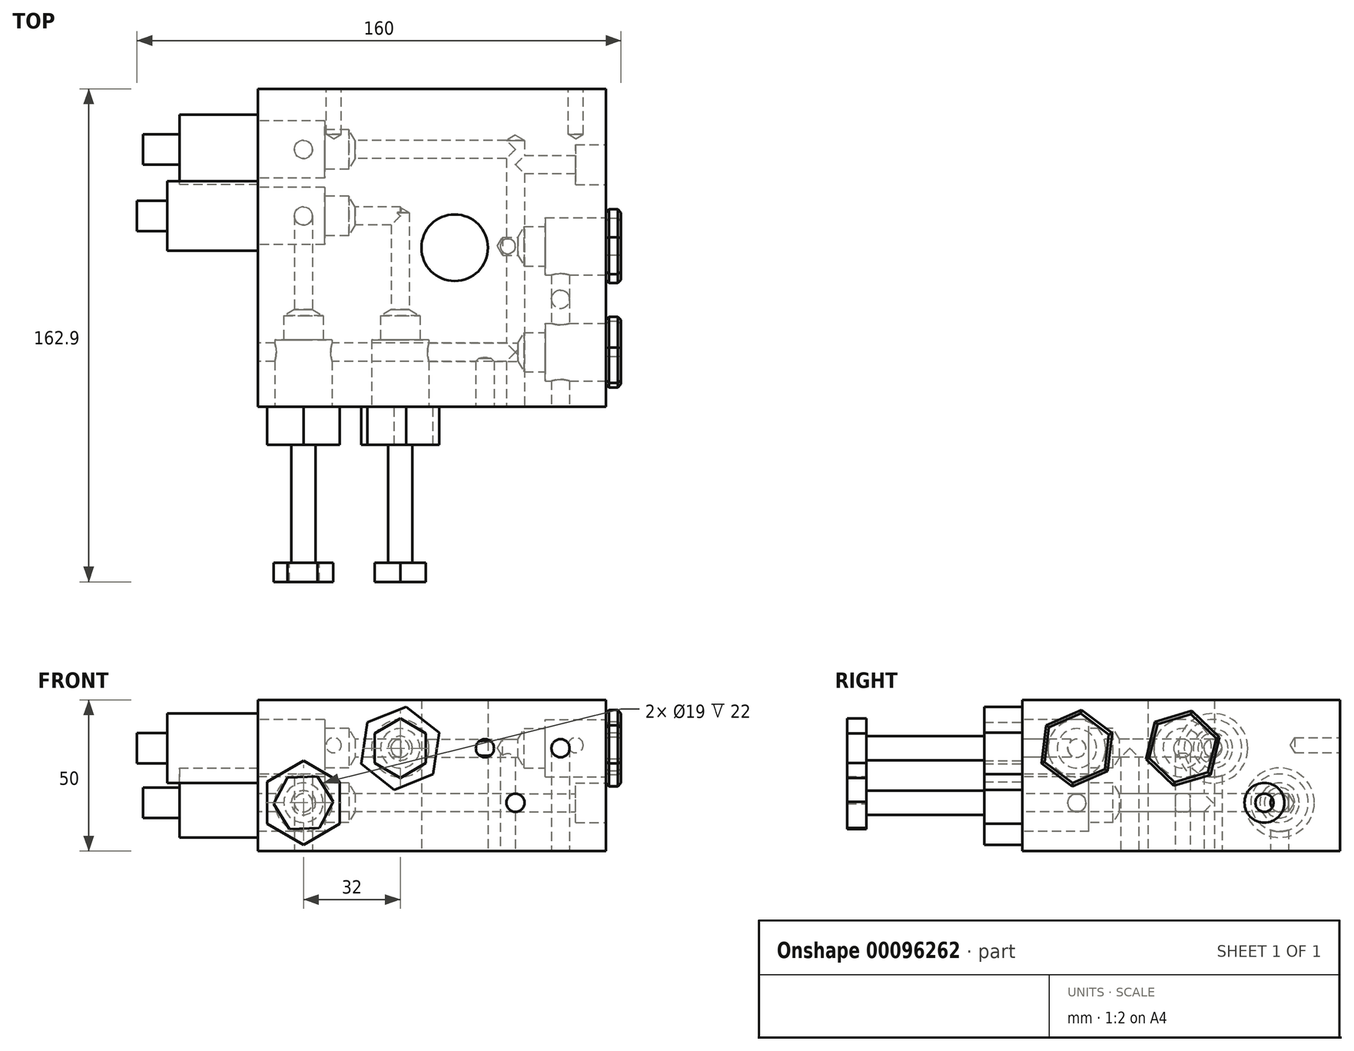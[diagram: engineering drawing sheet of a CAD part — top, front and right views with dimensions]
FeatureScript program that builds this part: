
annotation { "Feature Type Name" : "Feature", "Feature Type Description" : "" }
export const myFeature = defineFeature(function(context is Context, id is Id, definition is map)
    precondition{}
    {
        {
            var Q0;
            Q0=qCreatedBy(makeId("Top.planeOp"),FACE);
            var sketch = newSketch(context, id + "F0", { "sketchPlane" : qUnion([Q0])});
            skLineSegment(sketch, "E0.rect.bottom", {"start": v(50, 52.5) * mm, "end": v(-65, 52.5) * mm});
            skLineSegment(sketch, "E0.rect.top", {"start": v(50, -52.5) * mm, "end": v(-65, -52.5) * mm});
            skLineSegment(sketch, "E0.rect.left", {"start": v(50, 52.5) * mm, "end": v(50, -52.5) * mm});
            skLineSegment(sketch, "E0.rect.right", {"start": v(-65, 52.5) * mm, "end": v(-65, -52.5) * mm});
            skPoint(sketch, "E0.rect.middle", {"position": v(0, 0) * mm});
            skSolve(sketch);
        }
        {
            var Q0;
            Q0=makeQuery(id+"F0.imprint","IMPRINT",FACE,{"disambiguationData":[TD([[makeQuery(id+"F0.imprint","IMPRINT",EDGE,{"derivedFrom":sQuery(id+"F0.wireOp",EDGE,"E0.rect.bottom")}),1.0]])]});
            var Q1;
            Q1=makeQuery(id+"F0.imprint","IMPRINT",FACE,{"disambiguationData":[TD([[makeQuery(id+"F0.imprint","IMPRINT",EDGE,{"derivedFrom":sQuery(id+"F0.wireOp",EDGE,"7588558b-6d4b-4371-8287-17bf13519ebf.1.0.0")}),1.0]])]});
            var Q2;
            Q2=makeQuery(id+"F0.imprint","IMPRINT",FACE,{"disambiguationData":[TD([[makeQuery(id+"F0.imprint","IMPRINT",EDGE,{"derivedFrom":sQuery(id+"F0.wireOp",EDGE,"7588558b-6d4b-4371-8287-17bf13519ebf.1.1.0")}),1.0]])]});
            var Q3;
            Q3=makeQuery(id+"F0.imprint","IMPRINT",FACE,{"disambiguationData":[TD([[makeQuery(id+"F0.imprint","IMPRINT",EDGE,{"derivedFrom":sQuery(id+"F0.wireOp",EDGE,"f2f94a69-6f03-48d5-8e05-4ef8c2e551b9")}),1.0]])]});
            var Q4;
            Q4=makeQuery(id+"F0.imprint","IMPRINT",FACE,{"disambiguationData":[TD([[makeQuery(id+"F0.imprint","IMPRINT",EDGE,{"derivedFrom":sQuery(id+"F0.wireOp",EDGE,"7588558b-6d4b-4371-8287-17bf13519ebf.0.1.0")}),1.0]])]});
            extrude(context, id + "F1", {"entities" : qUnion([Q0, Q1, Q2, Q3, Q4]), "depth" : 50 * mm});
        }
        {
            var Q0;
            Q0=makeQuery(id+"F1.opExtrude","CAP_FACE",FACE,{"disambiguationData":[OSD([sQuery(id+"F0.wireOp",EDGE,"E0.rect.bottom"),sQuery(id+"F0.wireOp",EDGE,"E0.rect.top"),sQuery(id+"F0.wireOp",EDGE,"E0.rect.left"),sQuery(id+"F0.wireOp",EDGE,"E0.rect.right"),sQuery(id+"F0.wireOp",EDGE,"fc206ab4-4ad2-4e77-9b30-4fb9f0a5357b")])],"isStart":true});
            var sketch = newSketch(context, id + "F2", { "sketchPlane" : qUnion([Q0])});
            skCircle(sketch, "E1", {"center": v(11.74, 13.3) * mm, "radius": 2.1 * mm});
            skCircle(sketch, "E2", {"center": v(-6.03, -26.8) * mm, "radius": 2.1 * mm});
            skCircle(sketch, "E3", {"center": v(17.59, -0.5) * mm, "radius": 2.5 * mm});
            skPoint(sketch, "E4", {"position": v(-50, -10.5) * mm});
            skPoint(sketch, "E5", {"position": v(35, 17) * mm});
            skPoint(sketch, "E6", {"position": v(-50, -32.5) * mm});
            skSolve(sketch);
        }
        {
            var Q0;
            Q0=sQuery(id+"F2.wireOp",VERTEX,"E3.center");
            var Q1;
            Q1=makeQuery(id+"F1.opExtrude","SWEPT_BODY",BODY,{"disambiguationData":[OSD([sQuery(id+"F0.wireOp",EDGE,"E0.rect.bottom"),sQuery(id+"F0.wireOp",EDGE,"E0.rect.top"),sQuery(id+"F0.wireOp",EDGE,"E0.rect.left"),sQuery(id+"F0.wireOp",EDGE,"E0.rect.right"),sQuery(id+"F0.wireOp",EDGE,"fc206ab4-4ad2-4e77-9b30-4fb9f0a5357b")])]});
            hole(context, id + "F3", {"style" : HoleStyle.SIMPLE, "holeDiameter" : 5 * mm, "endStyle" : HoleEndStyle.BLIND, "holeDepth" : 35 * mm, "locations" : qUnion([Q0]), "scope" : qUnion([Q1])});
        }
        {
            var Q0;
            Q0=makeQuery(id+"F1.opExtrude","SWEPT_FACE",FACE,{"disambiguationData":[OSD([sQuery(id+"F0.wireOp",EDGE,"E0.rect.bottom")])]});
            var sketch = newSketch(context, id + "F4", { "sketchPlane" : qUnion([Q0])});
            skLineSegment(sketch, "E7", {"start": v(65, 16) * mm, "end": v(-50, 16) * mm, "construction": true});
            skPoint(sketch, "E8", {"position": v(-20.09, 16) * mm});
            skPoint(sketch, "E9", {"position": v(45, 16) * mm});
            skSolve(sketch);
        }
        {
            var Q0;
            Q0=makeQuery(id+"F1.opExtrude","SWEPT_FACE",FACE,{"disambiguationData":[OSD([sQuery(id+"F0.wireOp",EDGE,"E0.rect.left")])]});
            var sketch = newSketch(context, id + "F5", { "sketchPlane" : qUnion([Q0])});
            skLineSegment(sketch, "E10", {"start": v(-34.5, 34) * mm, "end": v(0.5, 34) * mm, "construction": true});
            skPoint(sketch, "E11", {"position": v(0.5, 34) * mm});
            skPoint(sketch, "E12", {"position": v(-34.5, 34) * mm});
            skPoint(sketch, "E13.orphan", {"position": v(52.5, 34) * mm});
            skPoint(sketch, "E14", {"position": v(27.5, 16) * mm});
            skCircle(sketch, "E15.cCircle", {"center": v(-34.5, 34) * mm, "radius": 11 * mm, "construction": true});
            skLineSegment(sketch, "E15.0", {"start": v(-44.69, 41.58) * mm, "end": v(-33.03, 46.62) * mm});
            skLineSegment(sketch, "E15.1", {"start": v(-33.03, 46.62) * mm, "end": v(-22.84, 39.03) * mm});
            skLineSegment(sketch, "E15.2", {"start": v(-22.84, 39.03) * mm, "end": v(-24.31, 26.42) * mm});
            skLineSegment(sketch, "E15.3", {"start": v(-24.31, 26.42) * mm, "end": v(-35.97, 21.38) * mm});
            skLineSegment(sketch, "E15.4", {"start": v(-35.97, 21.38) * mm, "end": v(-46.16, 28.97) * mm});
            skLineSegment(sketch, "E15.5", {"start": v(-46.16, 28.97) * mm, "end": v(-44.69, 41.58) * mm});
            skPoint(sketch, "E15.0.midPoint", {"position": v(-38.86, 44.1) * mm});
            skCircle(sketch, "E16.cCircle", {"center": v(0.5, 34) * mm, "radius": 11 * mm, "construction": true});
            skLineSegment(sketch, "E16.0", {"start": v(-8.7, 42.75) * mm, "end": v(3.48, 46.35) * mm});
            skLineSegment(sketch, "E16.1", {"start": v(3.48, 46.35) * mm, "end": v(12.68, 37.6) * mm});
            skLineSegment(sketch, "E16.2", {"start": v(12.68, 37.6) * mm, "end": v(9.7, 25.25) * mm});
            skLineSegment(sketch, "E16.3", {"start": v(9.7, 25.25) * mm, "end": v(-2.48, 21.65) * mm});
            skLineSegment(sketch, "E16.4", {"start": v(-2.48, 21.65) * mm, "end": v(-11.68, 30.4) * mm});
            skLineSegment(sketch, "E16.5", {"start": v(-11.68, 30.4) * mm, "end": v(-8.7, 42.75) * mm});
            skPoint(sketch, "E16.0.midPoint", {"position": v(-2.61, 44.55) * mm});
            skSolve(sketch);
        }
        {
            var Q0;
            Q0=sQuery(id+"F5.wireOp",VERTEX,"E11");
            var Q1;
            Q1=sQuery(id+"F5.wireOp",VERTEX,"E12");
            var Q2;
            Q2=makeQuery(id+"F1.opExtrude","SWEPT_BODY",BODY,{"disambiguationData":[OSD([sQuery(id+"F0.wireOp",EDGE,"E0.rect.bottom"),sQuery(id+"F0.wireOp",EDGE,"E0.rect.top"),sQuery(id+"F0.wireOp",EDGE,"E0.rect.left"),sQuery(id+"F0.wireOp",EDGE,"E0.rect.right"),sQuery(id+"F0.wireOp",EDGE,"fc206ab4-4ad2-4e77-9b30-4fb9f0a5357b")])]});
            hole(context, id + "F6", {"style" : HoleStyle.C_BORE, "endStyle" : HoleEndStyle.BLIND, "holeDiameter" : 13 * mm, "cBoreDiameter" : 19 * mm, "cBoreDepth" : 20 * mm, "holeDepth" : 27 * mm, "locations" : qUnion([Q0, Q1]), "scope" : qUnion([Q2])});
        }
        {
            var Q0;
            Q0=makeQuery(id+"F1.opExtrude","SWEPT_FACE",FACE,{"disambiguationData":[OSD([sQuery(id+"F0.wireOp",EDGE,"E0.rect.top")])]});
            var sketch = newSketch(context, id + "F7", { "sketchPlane" : qUnion([Q0])});
            skLineSegment(sketch, "E17", {"start": v(-65, 34) * mm, "end": v(50, 34) * mm, "construction": true});
            skLineSegment(sketch, "E18", {"start": v(-65, 16) * mm, "end": v(50, 16) * mm, "construction": true});
            skPoint(sketch, "E19", {"position": v(-50, 16) * mm});
            skPoint(sketch, "E20", {"position": v(-18, 34) * mm});
            skPoint(sketch, "E21", {"position": v(35, 34) * mm});
            skPoint(sketch, "E22", {"position": v(10, 34) * mm});
            skPoint(sketch, "E23", {"position": v(20.1, 16) * mm});
            skSolve(sketch);
        }
        {
            var Q0;
            Q0=sQuery(id+"F7.wireOp",VERTEX,"E23");
            var Q1;
            Q1=makeQuery(id+"F1.opExtrude","SWEPT_BODY",BODY,{"disambiguationData":[OSD([sQuery(id+"F0.wireOp",EDGE,"E0.rect.bottom"),sQuery(id+"F0.wireOp",EDGE,"E0.rect.top"),sQuery(id+"F0.wireOp",EDGE,"E0.rect.left"),sQuery(id+"F0.wireOp",EDGE,"E0.rect.right"),sQuery(id+"F0.wireOp",EDGE,"fc206ab4-4ad2-4e77-9b30-4fb9f0a5357b")])]});
            hole(context, id + "F8", {"style" : HoleStyle.SIMPLE, "holeDiameter" : 6 * mm, "endStyle" : HoleEndStyle.BLIND, "holeDepth" : 88 * mm, "locations" : qUnion([Q0]), "scope" : qUnion([Q1])});
        }
        {
            var Q0;
            Q0=makeQuery(id+"F1.opExtrude","SWEPT_FACE",FACE,{"disambiguationData":[OSD([sQuery(id+"F0.wireOp",EDGE,"E0.rect.right")])]});
            var sketch = newSketch(context, id + "F9", { "sketchPlane" : qUnion([Q0])});
            skPoint(sketch, "E24", {"position": v(34.5, 16) * mm});
            skPoint(sketch, "E25", {"position": v(-10.5, 34) * mm});
            skPoint(sketch, "E26", {"position": v(-32.5, 16) * mm});
            skCircle(sketch, "E27", {"center": v(-10.5, 34) * mm, "radius": 11.5 * mm});
            skSolve(sketch);
        }
        {
            var Q0;
            Q0=sQuery(id+"F9.wireOp",VERTEX,"E24");
            var Q1;
            Q1=makeQuery(id+"F1.opExtrude","SWEPT_BODY",BODY,{"disambiguationData":[OSD([sQuery(id+"F0.wireOp",EDGE,"E0.rect.bottom"),sQuery(id+"F0.wireOp",EDGE,"E0.rect.top"),sQuery(id+"F0.wireOp",EDGE,"E0.rect.left"),sQuery(id+"F0.wireOp",EDGE,"E0.rect.right"),sQuery(id+"F0.wireOp",EDGE,"fc206ab4-4ad2-4e77-9b30-4fb9f0a5357b")])]});
            hole(context, id + "F10", {"style" : HoleStyle.SIMPLE, "endStyle" : HoleEndStyle.BLIND, "holeDiameter" : 6 * mm, "holeDepth" : 86 * mm, "locations" : qUnion([Q0]), "scope" : qUnion([Q1])});
        }
        {
            var Q0;
            Q0=sQuery(id+"F7.wireOp",VERTEX,"E19");
            var Q1;
            Q1=sQuery(id+"F7.wireOp",VERTEX,"E20");
            var Q2;
            Q2=makeQuery(id+"F1.opExtrude","SWEPT_BODY",BODY,{"disambiguationData":[OSD([sQuery(id+"F0.wireOp",EDGE,"E0.rect.bottom"),sQuery(id+"F0.wireOp",EDGE,"E0.rect.top"),sQuery(id+"F0.wireOp",EDGE,"E0.rect.left"),sQuery(id+"F0.wireOp",EDGE,"E0.rect.right"),sQuery(id+"F0.wireOp",EDGE,"fc206ab4-4ad2-4e77-9b30-4fb9f0a5357b")])]});
            hole(context, id + "F11", {"style" : HoleStyle.C_BORE, "endStyle" : HoleEndStyle.BLIND, "holeDiameter" : 13 * mm, "cBoreDiameter" : 19 * mm, "cBoreDepth" : 22 * mm, "holeDepth" : 30 * mm, "locations" : qUnion([Q0, Q1]), "scope" : qUnion([Q2])});
        }
        {
            var Q0;
            Q0=sQuery(id+"F7.wireOp",VERTEX,"E19");
            var Q1;
            Q1=makeQuery(id+"F1.opExtrude","SWEPT_BODY",BODY,{"disambiguationData":[OSD([sQuery(id+"F0.wireOp",EDGE,"E0.rect.bottom"),sQuery(id+"F0.wireOp",EDGE,"E0.rect.top"),sQuery(id+"F0.wireOp",EDGE,"E0.rect.left"),sQuery(id+"F0.wireOp",EDGE,"E0.rect.right"),sQuery(id+"F0.wireOp",EDGE,"fc206ab4-4ad2-4e77-9b30-4fb9f0a5357b")])]});
            hole(context, id + "F12", {"style" : HoleStyle.SIMPLE, "endStyle" : HoleEndStyle.BLIND, "holeDiameter" : 6 * mm, "holeDepth" : 31 * mm, "locations" : qUnion([Q0]), "scope" : qUnion([Q1])});
        }
        {
            var Q0;
            Q0=sQuery(id+"F5.wireOp",VERTEX,"E11");
            var Q1;
            Q1=makeQuery(id+"F1.opExtrude","SWEPT_BODY",BODY,{"disambiguationData":[OSD([sQuery(id+"F0.wireOp",EDGE,"E0.rect.bottom"),sQuery(id+"F0.wireOp",EDGE,"E0.rect.top"),sQuery(id+"F0.wireOp",EDGE,"E0.rect.left"),sQuery(id+"F0.wireOp",EDGE,"E0.rect.right"),sQuery(id+"F0.wireOp",EDGE,"fc206ab4-4ad2-4e77-9b30-4fb9f0a5357b")])]});
            hole(context, id + "F13", {"style" : HoleStyle.SIMPLE, "endStyle" : HoleEndStyle.BLIND, "holeDiameter" : 6 * mm, "holeDepth" : 5 * mm, "locations" : qUnion([Q0]), "scope" : qUnion([Q1])});
        }
        {
            var Q0;
            Q0=sQuery(id+"F7.wireOp",VERTEX,"E22");
            var Q1;
            Q1=makeQuery(id+"F1.opExtrude","SWEPT_BODY",BODY,{"disambiguationData":[OSD([sQuery(id+"F0.wireOp",EDGE,"E0.rect.bottom"),sQuery(id+"F0.wireOp",EDGE,"E0.rect.top"),sQuery(id+"F0.wireOp",EDGE,"E0.rect.left"),sQuery(id+"F0.wireOp",EDGE,"E0.rect.right"),sQuery(id+"F0.wireOp",EDGE,"fc206ab4-4ad2-4e77-9b30-4fb9f0a5357b")])]});
            hole(context, id + "F14", {"style" : HoleStyle.SIMPLE, "endStyle" : HoleEndStyle.BLIND, "holeDiameter" : 6 * mm, "holeDepth" : 16 * mm, "locations" : qUnion([Q0]), "scope" : qUnion([Q1])});
        }
        {
            var Q0;
            Q0=sQuery(id+"F5.wireOp",VERTEX,"E12");
            var Q1;
            Q1=makeQuery(id+"F1.opExtrude","SWEPT_BODY",BODY,{"disambiguationData":[OSD([sQuery(id+"F0.wireOp",EDGE,"E0.rect.bottom"),sQuery(id+"F0.wireOp",EDGE,"E0.rect.top"),sQuery(id+"F0.wireOp",EDGE,"E0.rect.left"),sQuery(id+"F0.wireOp",EDGE,"E0.rect.right"),sQuery(id+"F0.wireOp",EDGE,"fc206ab4-4ad2-4e77-9b30-4fb9f0a5357b")])]});
            hole(context, id + "F15", {"style" : HoleStyle.SIMPLE, "endStyle" : HoleEndStyle.BLIND, "holeDiameter" : 6 * mm, "holeDepth" : 30 * mm, "locations" : qUnion([Q0]), "scope" : qUnion([Q1])});
        }
        {
            var Q0;
            Q0=sQuery(id+"F7.wireOp",VERTEX,"E21");
            var Q1;
            Q1=makeQuery(id+"F1.opExtrude","SWEPT_BODY",BODY,{"disambiguationData":[OSD([sQuery(id+"F0.wireOp",EDGE,"E0.rect.bottom"),sQuery(id+"F0.wireOp",EDGE,"E0.rect.top"),sQuery(id+"F0.wireOp",EDGE,"E0.rect.left"),sQuery(id+"F0.wireOp",EDGE,"E0.rect.right"),sQuery(id+"F0.wireOp",EDGE,"fc206ab4-4ad2-4e77-9b30-4fb9f0a5357b")])]});
            hole(context, id + "F16", {"style" : HoleStyle.SIMPLE, "endStyle" : HoleEndStyle.BLIND, "holeDiameter" : 6 * mm, "holeDepth" : 50 * mm, "locations" : qUnion([Q0]), "scope" : qUnion([Q1])});
        }
        {
            var Q0;
            Q0=sQuery(id+"F5.wireOp",VERTEX,"53e86b82-a842-4255-912a-a7488f70ac65");
            var Q1;
            Q1=sQuery(id+"F2.wireOp",VERTEX,"E5");
            var Q2;
            Q2=makeQuery(id+"F1.opExtrude","SWEPT_BODY",BODY,{"disambiguationData":[OSD([sQuery(id+"F0.wireOp",EDGE,"E0.rect.bottom"),sQuery(id+"F0.wireOp",EDGE,"E0.rect.top"),sQuery(id+"F0.wireOp",EDGE,"E0.rect.left"),sQuery(id+"F0.wireOp",EDGE,"E0.rect.right"),sQuery(id+"F0.wireOp",EDGE,"fc206ab4-4ad2-4e77-9b30-4fb9f0a5357b")])]});
            hole(context, id + "F17", {"style" : HoleStyle.SIMPLE, "endStyle" : HoleEndStyle.BLIND, "holeDiameter" : 6 * mm, "holeDepth" : 34 * mm, "locations" : qUnion([Q0, Q1]), "scope" : qUnion([Q2])});
        }
        {
            var Q0;
            Q0=sQuery(id+"F9.wireOp",VERTEX,"E25");
            var Q1;
            Q1=makeQuery(id+"F1.opExtrude","SWEPT_BODY",BODY,{"disambiguationData":[OSD([sQuery(id+"F0.wireOp",EDGE,"E0.rect.bottom"),sQuery(id+"F0.wireOp",EDGE,"E0.rect.top"),sQuery(id+"F0.wireOp",EDGE,"E0.rect.left"),sQuery(id+"F0.wireOp",EDGE,"E0.rect.right"),sQuery(id+"F0.wireOp",EDGE,"fc206ab4-4ad2-4e77-9b30-4fb9f0a5357b")])]});
            hole(context, id + "F18", {"style" : HoleStyle.C_BORE, "endStyle" : HoleEndStyle.BLIND, "holeDiameter" : 13 * mm, "cBoreDiameter" : 19 * mm, "cBoreDepth" : 22 * mm, "holeDepth" : 30 * mm, "locations" : qUnion([Q0]), "scope" : qUnion([Q1])});
        }
        {
            var Q0;
            Q0=sQuery(id+"F9.wireOp",VERTEX,"E25");
            var Q1;
            Q1=makeQuery(id+"F1.opExtrude","SWEPT_BODY",BODY,{"disambiguationData":[OSD([sQuery(id+"F0.wireOp",EDGE,"E0.rect.bottom"),sQuery(id+"F0.wireOp",EDGE,"E0.rect.top"),sQuery(id+"F0.wireOp",EDGE,"E0.rect.left"),sQuery(id+"F0.wireOp",EDGE,"E0.rect.right"),sQuery(id+"F0.wireOp",EDGE,"fc206ab4-4ad2-4e77-9b30-4fb9f0a5357b")])]});
            hole(context, id + "F19", {"style" : HoleStyle.SIMPLE, "endStyle" : HoleEndStyle.BLIND, "holeDiameter" : 6 * mm, "holeDepth" : 15 * mm, "locations" : qUnion([Q0]), "scope" : qUnion([Q1])});
        }
        {
            var Q0;
            Q0=sQuery(id+"F2.wireOp",VERTEX,"E4");
            var Q1;
            Q1=makeQuery(id+"F1.opExtrude","SWEPT_BODY",BODY,{"disambiguationData":[OSD([sQuery(id+"F0.wireOp",EDGE,"E0.rect.bottom"),sQuery(id+"F0.wireOp",EDGE,"E0.rect.top"),sQuery(id+"F0.wireOp",EDGE,"E0.rect.left"),sQuery(id+"F0.wireOp",EDGE,"E0.rect.right"),sQuery(id+"F0.wireOp",EDGE,"fc206ab4-4ad2-4e77-9b30-4fb9f0a5357b")])]});
            hole(context, id + "F20", {"style" : HoleStyle.SIMPLE, "endStyle" : HoleEndStyle.BLIND, "holeDiameter" : 6 * mm, "holeDepth" : 35 * mm, "locations" : qUnion([Q0]), "scope" : qUnion([Q1])});
        }
        {
            var Q0;
            Q0=sQuery(id+"F7.wireOp",VERTEX,"E20");
            var Q1;
            Q1=makeQuery(id+"F1.opExtrude","SWEPT_BODY",BODY,{"disambiguationData":[OSD([sQuery(id+"F0.wireOp",EDGE,"E0.rect.bottom"),sQuery(id+"F0.wireOp",EDGE,"E0.rect.top"),sQuery(id+"F0.wireOp",EDGE,"E0.rect.left"),sQuery(id+"F0.wireOp",EDGE,"E0.rect.right"),sQuery(id+"F0.wireOp",EDGE,"fc206ab4-4ad2-4e77-9b30-4fb9f0a5357b")])]});
            hole(context, id + "F21", {"style" : HoleStyle.SIMPLE, "endStyle" : HoleEndStyle.BLIND, "holeDiameter" : 6 * mm, "holeDepth" : 32 * mm, "locations" : qUnion([Q0]), "scope" : qUnion([Q1])});
        }
        {
            var Q0;
            Q0=makeQuery(id+"F1.opExtrude","SWEPT_FACE",FACE,{"disambiguationData":[OSD([sQuery(id+"F0.wireOp",EDGE,"E0.rect.bottom")])]});
            var sketch = newSketch(context, id + "F22", { "sketchPlane" : qUnion([Q0])});
            skPoint(sketch, "E28", {"position": v(-40, 35) * mm});
            skPoint(sketch, "E29.1.0.0", {"position": v(40, 35) * mm});
            skLineSegment(sketch, "E29.direction1", {"start": v(-40, 35) * mm, "end": v(40, 35) * mm, "construction": true});
            skSolve(sketch);
        }
        {
            var Q0;
            Q0=sQuery(id+"F22.wireOp",VERTEX,"E29.1.0.0");
            var Q1;
            Q1=sQuery(id+"F22.wireOp",VERTEX,"E28");
            var Q2;
            Q2=makeQuery(id+"F1.opExtrude","SWEPT_BODY",BODY,{"disambiguationData":[OSD([sQuery(id+"F0.wireOp",EDGE,"E0.rect.bottom"),sQuery(id+"F0.wireOp",EDGE,"E0.rect.top"),sQuery(id+"F0.wireOp",EDGE,"E0.rect.left"),sQuery(id+"F0.wireOp",EDGE,"E0.rect.right"),sQuery(id+"F0.wireOp",EDGE,"fc206ab4-4ad2-4e77-9b30-4fb9f0a5357b")])]});
            hole(context, id + "F23", {"style" : HoleStyle.SIMPLE, "endStyle" : HoleEndStyle.BLIND, "holeDiameter" : 5 * mm, "holeDepth" : 15 * mm, "locations" : qUnion([Q0, Q1]), "scope" : qUnion([Q2])});
        }
        {
            var Q0;
            Q0=sQuery(id+"F5.wireOp",VERTEX,"E14");
            var Q1;
            Q1=makeQuery(id+"F1.opExtrude","SWEPT_BODY",BODY,{"disambiguationData":[OSD([sQuery(id+"F0.wireOp",EDGE,"E0.rect.bottom"),sQuery(id+"F0.wireOp",EDGE,"E0.rect.top"),sQuery(id+"F0.wireOp",EDGE,"E0.rect.left"),sQuery(id+"F0.wireOp",EDGE,"E0.rect.right"),sQuery(id+"F0.wireOp",EDGE,"fc206ab4-4ad2-4e77-9b30-4fb9f0a5357b")])]});
            hole(context, id + "F24", {"style" : HoleStyle.C_BORE, "endStyle" : HoleEndStyle.BLIND, "holeDiameter" : 6 * mm, "cBoreDiameter" : 13.16 * mm, "cBoreDepth" : 10 * mm, "holeDepth" : 30 * mm, "locations" : qUnion([Q0]), "scope" : qUnion([Q1])});
        }
        {
            var Q0;
            Q0=sQuery(id+"F0.wireOp",VERTEX,"E0.rect.middle");
            var Q1;
            Q1=makeQuery(id+"F1.opExtrude","SWEPT_BODY",BODY,{"disambiguationData":[OSD([sQuery(id+"F0.wireOp",EDGE,"E0.rect.bottom"),sQuery(id+"F0.wireOp",EDGE,"E0.rect.top"),sQuery(id+"F0.wireOp",EDGE,"E0.rect.left"),sQuery(id+"F0.wireOp",EDGE,"E0.rect.right")])]});
            hole(context, id + "F25", {"style" : HoleStyle.SIMPLE, "endStyle" : HoleEndStyle.THROUGH, "oppositeDirection" : true, "holeDiameter" : 22 * mm, "locations" : qUnion([Q0]), "scope" : qUnion([Q1]), "isTappedThrough" : true});
        }
        {
            var Q0;
            {var subQ0=sQuery(id+"F0.wireOp",EDGE,"E0.rect.right");Q0=makeQuery(id+"F9.imprint","IMPRINT",FACE,{"disambiguationData":[TD([[makeQuery(id+"F9.imprint","IMPRINT",EDGE,{"derivedFrom":makeQuery(id+"F1.opExtrude","CAP_EDGE",EDGE,{"disambiguationData":[OSD([subQ0])],"isStart":true})}),1.0]])]});}
            var sketch = newSketch(context, id + "F26", { "sketchPlane" : qUnion([Q0])});
            skCircle(sketch, "E30", {"center": v(-32.5, 16) * mm, "radius": 11.5 * mm});
            skSolve(sketch);
        }
        {
            var Q0;
            Q0=makeQuery(id+"F26.imprint","IMPRINT",FACE,{"disambiguationData":[TD([[makeQuery(id+"F26.imprint","IMPRINT",EDGE,{"derivedFrom":sQuery(id+"F26.wireOp",EDGE,"E30")}),1.0]])]});
            extrude(context, id + "F27", {"entities" : qUnion([Q0]), "depth" : 26 * mm});
        }
        {
            var Q0;
            Q0=makeQuery(id+"F27.opExtrude","CAP_FACE",FACE,{"disambiguationData":[OSD([sQuery(id+"F26.wireOp",EDGE,"E30")])],"isStart":false});
            var sketch = newSketch(context, id + "F28", { "sketchPlane" : qUnion([Q0])});
            skCircle(sketch, "E31", {"center": v(-32.5, 16) * mm, "radius": 5 * mm});
            skSolve(sketch);
        }
        {
            var Q0;
            Q0=sQuery(id+"F9.wireOp",VERTEX,"E26");
            var Q1;
            Q1=makeQuery(id+"F1.opExtrude","SWEPT_BODY",BODY,{"disambiguationData":[OSD([sQuery(id+"F0.wireOp",EDGE,"E0.rect.bottom"),sQuery(id+"F0.wireOp",EDGE,"E0.rect.top"),sQuery(id+"F0.wireOp",EDGE,"E0.rect.left"),sQuery(id+"F0.wireOp",EDGE,"E0.rect.right")])]});
            hole(context, id + "F29", {"style" : HoleStyle.C_BORE, "endStyle" : HoleEndStyle.BLIND, "holeDiameter" : 13 * mm, "cBoreDiameter" : 19 * mm, "cBoreDepth" : 22 * mm, "holeDepth" : 30 * mm, "startFromSketch" : true, "locations" : qUnion([Q0]), "scope" : qUnion([Q1])});
        }
        {
            var Q0;
            Q0=sQuery(id+"F9.wireOp",VERTEX,"E26");
            var Q1;
            Q1=makeQuery(id+"F1.opExtrude","SWEPT_BODY",BODY,{"disambiguationData":[OSD([sQuery(id+"F0.wireOp",EDGE,"E0.rect.bottom"),sQuery(id+"F0.wireOp",EDGE,"E0.rect.top"),sQuery(id+"F0.wireOp",EDGE,"E0.rect.left"),sQuery(id+"F0.wireOp",EDGE,"E0.rect.right")])]});
            hole(context, id + "F30", {"style" : HoleStyle.SIMPLE, "endStyle" : HoleEndStyle.BLIND, "holeDiameter" : 6 * mm, "holeDepth" : 85 * mm, "startFromSketch" : true, "locations" : qUnion([Q0]), "scope" : qUnion([Q1])});
        }
        {
            var Q0;
            Q0=makeQuery(id+"F5.imprint","IMPRINT",FACE,{"disambiguationData":[TD([[makeQuery(id+"F5.imprint","IMPRINT",EDGE,{"derivedFrom":sQuery(id+"F5.wireOp",EDGE,"E15.0")}),-1.0]])]});
            var Q1;
            Q1=makeQuery(id+"F5.imprint","IMPRINT",FACE,{"disambiguationData":[TD([[makeQuery(id+"F5.imprint","IMPRINT",EDGE,{"derivedFrom":sQuery(id+"F5.wireOp",EDGE,"E16.0")}),-1.0]])]});
            extrude(context, id + "F31", {"entities" : qUnion([Q0, Q1]), "depth" : 5 * mm});
        }
        {
            var Q0;
            Q0=makeQuery(id+"F31.opExtrude","CAP_EDGE",EDGE,{"disambiguationData":[OSD([sQuery(id+"F5.wireOp",EDGE,"E15.3")])],"isStart":true});
            var Q1;
            Q1=makeQuery(id+"F31.opExtrude","CAP_EDGE",EDGE,{"disambiguationData":[OSD([sQuery(id+"F5.wireOp",EDGE,"E15.4")])],"isStart":true});
            var Q2;
            Q2=makeQuery(id+"F31.opExtrude","CAP_EDGE",EDGE,{"disambiguationData":[OSD([sQuery(id+"F5.wireOp",EDGE,"E15.5")])],"isStart":true});
            var Q3;
            Q3=makeQuery(id+"F31.opExtrude","CAP_EDGE",EDGE,{"disambiguationData":[OSD([sQuery(id+"F5.wireOp",EDGE,"E15.4")])],"isStart":false});
            var Q4;
            Q4=makeQuery(id+"F31.opExtrude","CAP_EDGE",EDGE,{"disambiguationData":[OSD([sQuery(id+"F5.wireOp",EDGE,"E15.3")])],"isStart":false});
            var Q5;
            Q5=makeQuery(id+"F31.opExtrude","CAP_EDGE",EDGE,{"disambiguationData":[OSD([sQuery(id+"F5.wireOp",EDGE,"E15.2")])],"isStart":false});
            var Q6;
            Q6=makeQuery(id+"F31.opExtrude","CAP_EDGE",EDGE,{"disambiguationData":[OSD([sQuery(id+"F5.wireOp",EDGE,"E15.1")])],"isStart":false});
            var Q7;
            Q7=makeQuery(id+"F31.opExtrude","CAP_EDGE",EDGE,{"disambiguationData":[OSD([sQuery(id+"F5.wireOp",EDGE,"E15.0")])],"isStart":false});
            var Q8;
            Q8=makeQuery(id+"F31.opExtrude","CAP_EDGE",EDGE,{"disambiguationData":[OSD([sQuery(id+"F5.wireOp",EDGE,"E15.5")])],"isStart":false});
            var Q9;
            Q9=makeQuery(id+"F31.opExtrude","CAP_EDGE",EDGE,{"disambiguationData":[OSD([sQuery(id+"F5.wireOp",EDGE,"E15.0")])],"isStart":true});
            var Q10;
            Q10=makeQuery(id+"F31.opExtrude","CAP_EDGE",EDGE,{"disambiguationData":[OSD([sQuery(id+"F5.wireOp",EDGE,"E15.1")])],"isStart":true});
            var Q11;
            Q11=makeQuery(id+"F31.opExtrude","CAP_EDGE",EDGE,{"disambiguationData":[OSD([sQuery(id+"F5.wireOp",EDGE,"E15.2")])],"isStart":true});
            var Q12;
            Q12=makeQuery(id+"F31.opExtrude","CAP_EDGE",EDGE,{"disambiguationData":[OSD([sQuery(id+"F5.wireOp",EDGE,"E16.4")])],"isStart":false});
            var Q13;
            Q13=makeQuery(id+"F31.opExtrude","CAP_EDGE",EDGE,{"disambiguationData":[OSD([sQuery(id+"F5.wireOp",EDGE,"E16.4")])],"isStart":true});
            var Q14;
            Q14=makeQuery(id+"F31.opExtrude","CAP_EDGE",EDGE,{"disambiguationData":[OSD([sQuery(id+"F5.wireOp",EDGE,"E16.3")])],"isStart":false});
            var Q15;
            Q15=makeQuery(id+"F31.opExtrude","CAP_EDGE",EDGE,{"disambiguationData":[OSD([sQuery(id+"F5.wireOp",EDGE,"E16.3")])],"isStart":true});
            var Q16;
            Q16=makeQuery(id+"F31.opExtrude","CAP_EDGE",EDGE,{"disambiguationData":[OSD([sQuery(id+"F5.wireOp",EDGE,"E16.2")])],"isStart":false});
            var Q17;
            Q17=makeQuery(id+"F31.opExtrude","CAP_EDGE",EDGE,{"disambiguationData":[OSD([sQuery(id+"F5.wireOp",EDGE,"E16.2")])],"isStart":true});
            var Q18;
            Q18=makeQuery(id+"F31.opExtrude","CAP_EDGE",EDGE,{"disambiguationData":[OSD([sQuery(id+"F5.wireOp",EDGE,"E16.1")])],"isStart":false});
            var Q19;
            Q19=makeQuery(id+"F31.opExtrude","CAP_EDGE",EDGE,{"disambiguationData":[OSD([sQuery(id+"F5.wireOp",EDGE,"E16.1")])],"isStart":true});
            var Q20;
            Q20=makeQuery(id+"F31.opExtrude","CAP_EDGE",EDGE,{"disambiguationData":[OSD([sQuery(id+"F5.wireOp",EDGE,"E16.5")])],"isStart":false});
            var Q21;
            Q21=makeQuery(id+"F31.opExtrude","CAP_EDGE",EDGE,{"disambiguationData":[OSD([sQuery(id+"F5.wireOp",EDGE,"E16.5")])],"isStart":true});
            var Q22;
            Q22=makeQuery(id+"F31.opExtrude","CAP_EDGE",EDGE,{"disambiguationData":[OSD([sQuery(id+"F5.wireOp",EDGE,"E16.0")])],"isStart":true});
            var Q23;
            Q23=makeQuery(id+"F31.opExtrude","CAP_EDGE",EDGE,{"disambiguationData":[OSD([sQuery(id+"F5.wireOp",EDGE,"E16.0")])],"isStart":false});
            chamfer(context, id + "F32", {"entities" : qUnion([Q0, Q1, Q2, Q3, Q4, Q5, Q6, Q7, Q8, Q9, Q10, Q11, Q12, Q13, Q14, Q15, Q16, Q17, Q18, Q19, Q20, Q21, Q22, Q23]), "width" : 1 * mm, "tangentPropagation" : true});
        }
        {
            var Q0;
            Q0=makeQuery(id+"F28.imprint","IMPRINT",FACE,{"disambiguationData":[TD([[makeQuery(id+"F28.imprint","IMPRINT",EDGE,{"derivedFrom":sQuery(id+"F28.wireOp",EDGE,"E31")}),1.0]])]});
            extrude(context, id + "F33", {"entities" : qUnion([Q0]), "operationType" : NewBodyOperationType.ADD, "depth" : 12 * mm});
        }
        {
            var Q0;
            Q0=makeQuery(id+"F9.imprint","IMPRINT",FACE,{"disambiguationData":[TD([[makeQuery(id+"F9.imprint","IMPRINT",EDGE,{"derivedFrom":sQuery(id+"F9.wireOp",EDGE,"E27")}),1.0]])]});
            extrude(context, id + "F34", {"entities" : qUnion([Q0]), "depth" : 30 * mm});
        }
        {
            var Q0;
            Q0=makeQuery(id+"F34.opExtrude","CAP_FACE",FACE,{"disambiguationData":[OSD([sQuery(id+"F9.wireOp",EDGE,"E27")])],"isStart":false});
            var sketch = newSketch(context, id + "F35", { "sketchPlane" : qUnion([Q0])});
            skCircle(sketch, "E32", {"center": v(-10.5, 34) * mm, "radius": 5 * mm});
            skSolve(sketch);
        }
        {
            var Q0;
            Q0=makeQuery(id+"F35.imprint","IMPRINT",FACE,{"disambiguationData":[TD([[makeQuery(id+"F35.imprint","IMPRINT",EDGE,{"derivedFrom":sQuery(id+"F35.wireOp",EDGE,"E32")}),1.0]])]});
            extrude(context, id + "F36", {"entities" : qUnion([Q0]), "operationType" : NewBodyOperationType.ADD, "depth" : 10 * mm});
        }
        {
            var Q0;
            Q0=sQuery(id+"F2.wireOp",VERTEX,"E6");
            var Q1;
            Q1=makeQuery(id+"F1.opExtrude","SWEPT_BODY",BODY,{"disambiguationData":[OSD([sQuery(id+"F0.wireOp",EDGE,"E0.rect.bottom"),sQuery(id+"F0.wireOp",EDGE,"E0.rect.top"),sQuery(id+"F0.wireOp",EDGE,"E0.rect.left"),sQuery(id+"F0.wireOp",EDGE,"E0.rect.right")])]});
            hole(context, id + "F37", {"style" : HoleStyle.SIMPLE, "endStyle" : HoleEndStyle.BLIND, "holeDiameter" : 6 * mm, "holeDepth" : 18 * mm, "locations" : qUnion([Q0]), "scope" : qUnion([Q1])});
        }
        {
            var Q0;
            {var subQ0=sQuery(id+"F0.wireOp",EDGE,"E0.rect.top");Q0=makeQuery(id+"F7.imprint","IMPRINT",FACE,{"disambiguationData":[TD([[makeQuery(id+"F7.imprint","IMPRINT",EDGE,{"derivedFrom":makeQuery(id+"F1.opExtrude","CAP_EDGE",EDGE,{"disambiguationData":[OSD([subQ0])],"isStart":true})}),-1.0]])]});}
            var sketch = newSketch(context, id + "F38", { "sketchPlane" : qUnion([Q0])});
            skCircle(sketch, "E33.cCircle", {"center": v(-50, 16) * mm, "radius": 12 * mm, "construction": true});
            skLineSegment(sketch, "E33.0", {"start": v(-38, 22.93) * mm, "end": v(-38, 9.07) * mm});
            skLineSegment(sketch, "E33.1", {"start": v(-38, 9.07) * mm, "end": v(-50, 2.14) * mm});
            skLineSegment(sketch, "E33.2", {"start": v(-50, 2.14) * mm, "end": v(-62, 9.07) * mm});
            skLineSegment(sketch, "E33.3", {"start": v(-62, 9.07) * mm, "end": v(-62, 22.93) * mm});
            skLineSegment(sketch, "E33.4", {"start": v(-62, 22.93) * mm, "end": v(-50, 29.86) * mm});
            skLineSegment(sketch, "E33.5", {"start": v(-50, 29.86) * mm, "end": v(-38, 22.93) * mm});
            skPoint(sketch, "E33.0.midPoint", {"position": v(-38, 16) * mm});
            skCircle(sketch, "E34.cCircle", {"center": v(-18, 34) * mm, "radius": 12 * mm, "construction": true});
            skLineSegment(sketch, "E34.0", {"start": v(-5.15, 39.18) * mm, "end": v(-7.1, 25.46) * mm});
            skLineSegment(sketch, "E34.1", {"start": v(-7.1, 25.46) * mm, "end": v(-19.94, 20.28) * mm});
            skLineSegment(sketch, "E34.2", {"start": v(-19.94, 20.28) * mm, "end": v(-30.85, 28.82) * mm});
            skLineSegment(sketch, "E34.3", {"start": v(-30.85, 28.82) * mm, "end": v(-28.9, 42.54) * mm});
            skLineSegment(sketch, "E34.4", {"start": v(-28.9, 42.54) * mm, "end": v(-16.06, 47.72) * mm});
            skLineSegment(sketch, "E34.5", {"start": v(-16.06, 47.72) * mm, "end": v(-5.15, 39.18) * mm});
            skPoint(sketch, "E34.0.midPoint", {"position": v(-6.12, 32.32) * mm});
            skSolve(sketch);
        }
        {
            var Q0;
            Q0=qSketchRegion(id+"F38",true);
            extrude(context, id + "F39", {"entities" : qUnion([Q0]), "depth" : 12.6 * mm});
        }
        {
            var Q0;
            Q0=makeQuery(id+"F39.opExtrude","CAP_FACE",FACE,{"disambiguationData":[OSD([sQuery(id+"F38.wireOp",EDGE,"E33.0"),sQuery(id+"F38.wireOp",EDGE,"E33.1"),sQuery(id+"F38.wireOp",EDGE,"E33.2"),sQuery(id+"F38.wireOp",EDGE,"E33.3"),sQuery(id+"F38.wireOp",EDGE,"E33.4"),sQuery(id+"F38.wireOp",EDGE,"E33.5")])],"isStart":false});
            var sketch = newSketch(context, id + "F40", { "sketchPlane" : qUnion([Q0])});
            skCircle(sketch, "E35", {"center": v(-50, 16) * mm, "radius": 4 * mm});
            skPoint(sketch, "E35.centerSnap0", {"position": v(-62, 16) * mm});
            skSolve(sketch);
        }
        {
            var Q0;
            Q0=makeQuery(id+"F40.imprint","IMPRINT",FACE,{"disambiguationData":[TD([[makeQuery(id+"F40.imprint","IMPRINT",EDGE,{"derivedFrom":sQuery(id+"F40.wireOp",EDGE,"E35")}),1.0]])]});
            extrude(context, id + "F41", {"entities" : qUnion([Q0]), "operationType" : NewBodyOperationType.ADD, "depth" : 39 * mm});
        }
        {
            var Q0;
            Q0=makeQuery(id+"F41.opExtrude","CAP_FACE",FACE,{"disambiguationData":[OSD([sQuery(id+"F40.wireOp",EDGE,"E35")])],"isStart":false});
            var sketch = newSketch(context, id + "F42", { "sketchPlane" : qUnion([Q0])});
            skCircle(sketch, "E36.cCircle", {"center": v(-50, 16) * mm, "radius": 8.5 * mm, "construction": true});
            skLineSegment(sketch, "E36.0", {"start": v(-45.41, 24.68) * mm, "end": v(-40.2, 16.37) * mm});
            skLineSegment(sketch, "E36.1", {"start": v(-40.2, 16.37) * mm, "end": v(-44.78, 7.69) * mm});
            skLineSegment(sketch, "E36.2", {"start": v(-44.78, 7.69) * mm, "end": v(-54.59, 7.32) * mm});
            skLineSegment(sketch, "E36.3", {"start": v(-54.59, 7.32) * mm, "end": v(-59.8, 15.63) * mm});
            skLineSegment(sketch, "E36.4", {"start": v(-59.8, 15.63) * mm, "end": v(-55.22, 24.31) * mm});
            skLineSegment(sketch, "E36.5", {"start": v(-55.22, 24.31) * mm, "end": v(-45.41, 24.68) * mm});
            skPoint(sketch, "E36.0.midPoint", {"position": v(-42.8, 20.52) * mm});
            skSolve(sketch);
        }
        {
            var Q0;
            Q0=makeQuery(id+"F42.imprint","IMPRINT",FACE,{"disambiguationData":[TD([[makeQuery(id+"F42.imprint","IMPRINT",EDGE,{"derivedFrom":sQuery(id+"F42.wireOp",EDGE,"E36.0")}),-1.0]])]});
            var Q1;
            Q1=makeQuery(id+"F42.imprint","IMPRINT",FACE,{"disambiguationData":[TD([[makeQuery(id+"F42.imprint","IMPRINT",EDGE,{"derivedFrom":makeQuery(id+"F41.opExtrude","CAP_EDGE",EDGE,{"disambiguationData":[OSD([sQuery(id+"F40.wireOp",EDGE,"E35")])],"isStart":false})}),1.0]])]});
            extrude(context, id + "F43", {"entities" : qUnion([Q0, Q1]), "operationType" : NewBodyOperationType.ADD, "depth" : 6.3 * mm});
        }
        {
            var Q0;
            Q0=makeQuery(id+"F39.opExtrude","CAP_FACE",FACE,{"disambiguationData":[OSD([sQuery(id+"F38.wireOp",EDGE,"E34.0"),sQuery(id+"F38.wireOp",EDGE,"E34.1"),sQuery(id+"F38.wireOp",EDGE,"E34.2"),sQuery(id+"F38.wireOp",EDGE,"E34.3"),sQuery(id+"F38.wireOp",EDGE,"E34.4"),sQuery(id+"F38.wireOp",EDGE,"E34.5")])],"isStart":false});
            var sketch = newSketch(context, id + "F44", { "sketchPlane" : qUnion([Q0])});
            skLineSegment(sketch, "E37", {"start": v(-13.52, 22.87) * mm, "end": v(-22.48, 45.13) * mm, "construction": true});
            skCircle(sketch, "E38", {"center": v(-18, 34) * mm, "radius": 4 * mm});
            skSolve(sketch);
        }
        {
            var Q0;
            Q0=makeQuery(id+"F44.imprint","IMPRINT",FACE,{"disambiguationData":[TD([[makeQuery(id+"F44.imprint","IMPRINT",EDGE,{"derivedFrom":sQuery(id+"F44.wireOp",EDGE,"E38")}),1.0]])]});
            extrude(context, id + "F45", {"entities" : qUnion([Q0]), "operationType" : NewBodyOperationType.ADD, "depth" : 39 * mm});
        }
        {
            var Q0;
            Q0=makeQuery(id+"F45.opExtrude","CAP_FACE",FACE,{"disambiguationData":[OSD([sQuery(id+"F44.wireOp",EDGE,"E38")])],"isStart":false});
            var sketch = newSketch(context, id + "F46", { "sketchPlane" : qUnion([Q0])});
            skCircle(sketch, "E39.cCircle", {"center": v(-18, 34) * mm, "radius": 8.5 * mm, "construction": true});
            skLineSegment(sketch, "E39.0", {"start": v(-9.5, 38.9) * mm, "end": v(-9.5, 29.1) * mm});
            skLineSegment(sketch, "E39.1", {"start": v(-9.5, 29.1) * mm, "end": v(-18, 24.19) * mm});
            skLineSegment(sketch, "E39.2", {"start": v(-18, 24.19) * mm, "end": v(-26.5, 29.1) * mm});
            skLineSegment(sketch, "E39.3", {"start": v(-26.5, 29.1) * mm, "end": v(-26.5, 38.9) * mm});
            skLineSegment(sketch, "E39.4", {"start": v(-26.5, 38.9) * mm, "end": v(-18, 43.81) * mm});
            skLineSegment(sketch, "E39.5", {"start": v(-18, 43.81) * mm, "end": v(-9.5, 38.9) * mm});
            skPoint(sketch, "E39.0.midPoint", {"position": v(-9.5, 34) * mm});
            skSolve(sketch);
        }
        {
            var Q0;
            Q0=makeQuery(id+"F46.imprint","IMPRINT",FACE,{"disambiguationData":[TD([[makeQuery(id+"F46.imprint","IMPRINT",EDGE,{"derivedFrom":sQuery(id+"F46.wireOp",EDGE,"E39.0")}),-1.0]])]});
            var Q1;
            Q1=makeQuery(id+"F46.imprint","IMPRINT",FACE,{"disambiguationData":[TD([[makeQuery(id+"F46.imprint","IMPRINT",EDGE,{"derivedFrom":makeQuery(id+"F45.opExtrude","CAP_EDGE",EDGE,{"disambiguationData":[OSD([sQuery(id+"F44.wireOp",EDGE,"E38")])],"isStart":false})}),1.0]])]});
            extrude(context, id + "F47", {"entities" : qUnion([Q0, Q1]), "operationType" : NewBodyOperationType.ADD, "depth" : 6.3 * mm});
        }
    });
